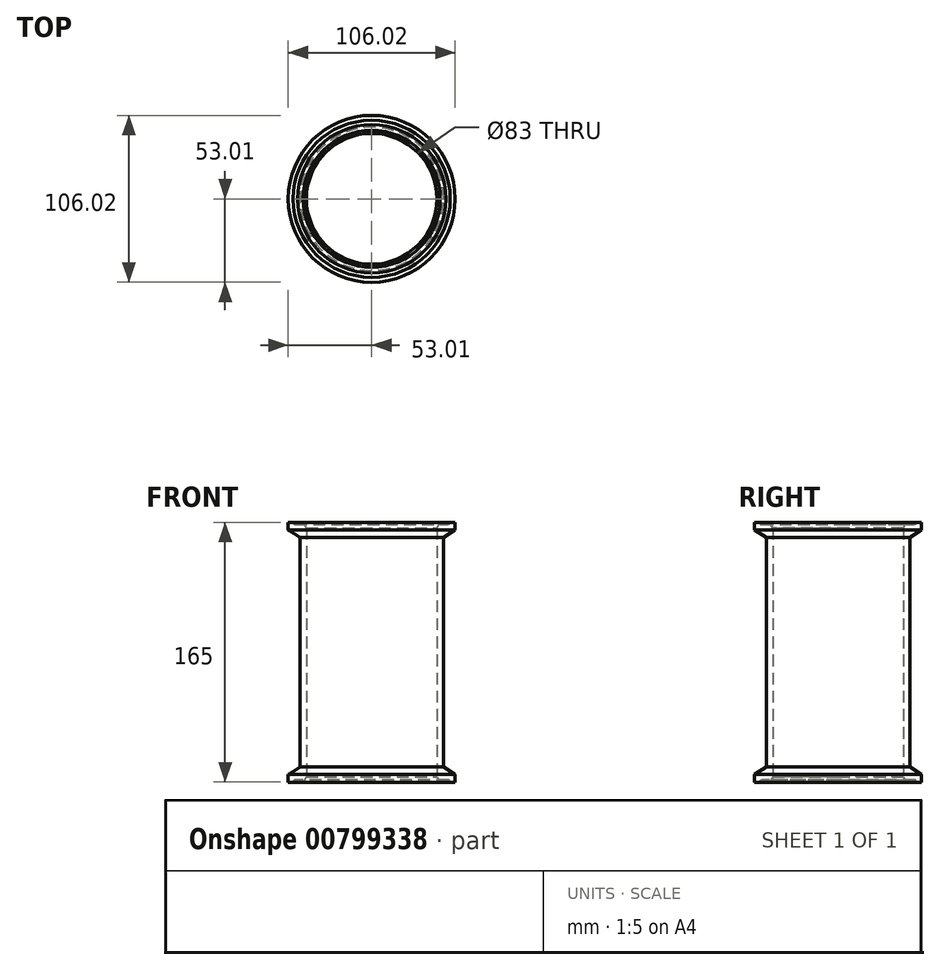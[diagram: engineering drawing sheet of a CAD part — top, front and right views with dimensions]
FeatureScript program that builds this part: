
annotation { "Feature Type Name" : "Feature", "Feature Type Description" : "" }
export const myFeature = defineFeature(function(context is Context, id is Id, definition is map)
    precondition{}
    {
        {
            var Q0;
            Q0=qCreatedBy(makeId("Front.planeOp"),FACE);
            var sketch = newSketch(context, id + "F0", { "sketchPlane" : qUnion([Q0])});
            skLineSegment(sketch, "E0", {"start": v(-45.5, -2.06) * mm, "end": v(-47.15, -2.06) * mm});
            skLineSegment(sketch, "E1", {"start": v(-45.5, 7.54) * mm, "end": v(-45.5, 18.94) * mm});
            skLineSegment(sketch, "E2", {"start": v(-49, 19.2) * mm, "end": v(-45.5, 18.94) * mm});
            skLineSegment(sketch, "E3", {"start": v(-53.01, -2.06) * mm, "end": v(-53.01, 2.74) * mm});
            skPoint(sketch, "E3.endSnap0", {"position": v(-45.5, 2.74) * mm});
            skLineSegment(sketch, "E4", {"start": v(-45.5, 7.54) * mm, "end": v(-53.01, 2.74) * mm});
            skArc(sketch, "E5", {"start": v(-47.15, -2.06) * mm, "mid": v(-48.51, -0.7) * mm, "end": v(-49.88, -2.06) * mm});
            skLineSegment(sketch, "E6.trimOffspring", {"start": v(-49.88, -2.06) * mm, "end": v(-53.01, -2.06) * mm});
            skLineSegment(sketch, "E7", {"start": v(0, 0) * mm, "end": v(0, 38.79) * mm, "construction": true});
            skLineSegment(sketch, "E8", {"start": v(0, -2.06) * mm, "end": v(-49, -2.06) * mm});
            skLineSegment(sketch, "E9", {"start": v(-45.5, -2.06) * mm, "end": v(-45.5, 2.2) * mm});
            skLineSegment(sketch, "E10.trimOffspring", {"start": v(-45.5, -2.06) * mm, "end": v(-45.5, -2.06) * mm});
            skLineSegment(sketch, "E11", {"start": v(-41.5, -2.06) * mm, "end": v(-41.5, 80.44) * mm});
            skLineSegment(sketch, "E12", {"start": v(-41.5, -2.06) * mm, "end": v(-45.5, -2.06) * mm});
            skLineSegment(sketch, "E13", {"start": v(-45.5, 18.94) * mm, "end": v(-45.5, 80.44) * mm});
            skLineSegment(sketch, "E14", {"start": v(-45.5, 80.44) * mm, "end": v(-41.5, 80.44) * mm});
            skLineSegment(sketch, "E15.MirrorCS", {"start": v(-45.5, 141.94) * mm, "end": v(-45.5, 80.44) * mm});
            skLineSegment(sketch, "E16.MirrorCS", {"start": v(-45.5, 153.34) * mm, "end": v(-45.5, 141.94) * mm});
            skLineSegment(sketch, "E17.MirrorCS", {"start": v(-45.5, 153.34) * mm, "end": v(-53.01, 158.14) * mm});
            skLineSegment(sketch, "E18.MirrorCS", {"start": v(-53.01, 162.94) * mm, "end": v(-53.01, 158.14) * mm});
            skLineSegment(sketch, "E19.MirrorCS", {"start": v(-49.88, 162.94) * mm, "end": v(-53.01, 162.94) * mm});
            skArc(sketch, "E20.MirrorCS", {"start": v(-47.15, 162.94) * mm, "mid": v(-48.51, 161.57) * mm, "end": v(-49.88, 162.94) * mm});
            skLineSegment(sketch, "E21.MirrorCS", {"start": v(-45.5, 162.94) * mm, "end": v(-47.15, 162.94) * mm});
            skLineSegment(sketch, "E22.MirrorCS", {"start": v(-41.5, 162.94) * mm, "end": v(-45.5, 162.94) * mm});
            skLineSegment(sketch, "E23.MirrorCS", {"start": v(-41.5, 162.94) * mm, "end": v(-41.5, 80.44) * mm});
            skLineSegment(sketch, "E24", {"start": v(0, -2.06) * mm, "end": v(0, -9.88) * mm});
            skLineSegment(sketch, "E25", {"start": v(0, -9.88) * mm, "end": v(-50, -9.88) * mm});
            skSolve(sketch);
        }
        {
            var Q0;
            Q0=qSketchRegion(id+"F0",true);
            var Q1;
            Q1=sQuery(id+"F0.wireOp",EDGE,"E7");
            revolve(context, id + "F1", {"entities" : qUnion([Q0]), "axis" : qUnion([Q1]), "revolveType" : RevolveType.FULL});
        }
        {
            var Q0;
            Q0=makeQuery(id+"F1.opRevolve","SWEPT_EDGE",EDGE,{"disambiguationData":[OSD([sQuery(id+"F0.wireOp",EDGE,"E22.MirrorCS"),sQuery(id+"F0.wireOp",EDGE,"E23.MirrorCS")])]});
            var Q1;
            Q1=makeQuery(id+"F1.opRevolve","SWEPT_EDGE",EDGE,{"disambiguationData":[OSD([sQuery(id+"F0.wireOp",EDGE,"E11"),sQuery(id+"F0.wireOp",EDGE,"E12")])]});
            chamfer(context, id + "F2", {"entities" : qUnion([Q0, Q1]), "chamferType" : ChamferType.OFFSET_ANGLE, "width" : 2 * mm, "oppositeDirection" : false, "angle" : 60 * degree, "tangentPropagation" : true});
        }
    });
